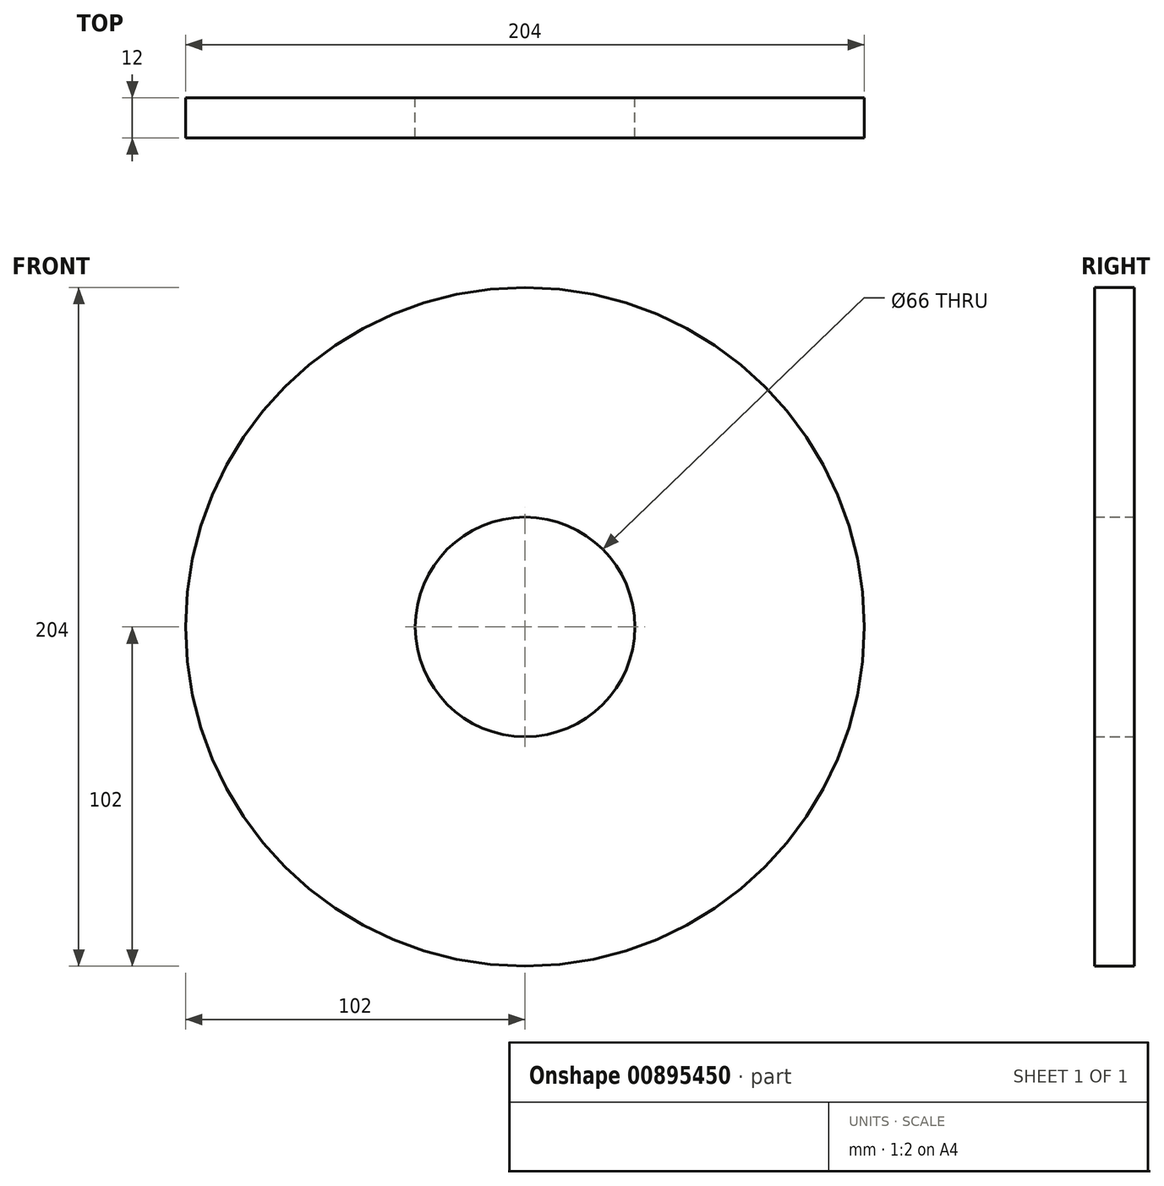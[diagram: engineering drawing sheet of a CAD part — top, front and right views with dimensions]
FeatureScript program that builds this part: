
annotation { "Feature Type Name" : "Feature", "Feature Type Description" : "" }
export const myFeature = defineFeature(function(context is Context, id is Id, definition is map)
    precondition{}
    {
        {
            var Q0;
            Q0=qCreatedBy(makeId("Front.planeOp"),FACE);
            var sketch = newSketch(context, id + "F0", { "sketchPlane" : qUnion([Q0])});
            skCircle(sketch, "E0", {"center": v(0, 0) * mm, "radius": 33 * mm});
            skCircle(sketch, "E1", {"center": v(0, 0) * mm, "radius": 102 * mm});
            skSolve(sketch);
        }
        {
            var Q0;
            Q0=makeQuery(id+"F0.imprint","IMPRINT",FACE,{"disambiguationData":[TD([[makeQuery(id+"F0.imprint","IMPRINT",EDGE,{"derivedFrom":sQuery(id+"F0.wireOp",EDGE,"E0")}),-1.0]])]});
            extrude(context, id + "F1", {"entities" : qUnion([Q0]), "depth" : 12 * mm, "offsetDistance" : 25 * mm});
        }
    });
